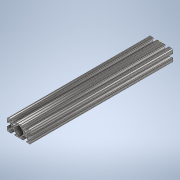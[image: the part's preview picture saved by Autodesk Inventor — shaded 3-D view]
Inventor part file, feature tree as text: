
AUTODESK INVENTOR PART (.ipt)
format: ipt  version: 2020 (Build 240168000, 168)  size: 344,576 bytes
history: native  units: in
note: dims shown in document units (in); Inventor stores cm internally (conversion verified against a paired STEP export)
features: sketch x2, extrude x1
ambient origin geometry x8: Origin, YZ Plane, XZ Plane, XY Plane, X Axis, Y Axis, Z Axis, Center Point
bodies: Solid1 (feature_tree)
feature tree (3):
  extrude  "Extrusion1"  [1 undecoded]
  sketch  "Sketch2"
  sketch  "Sketch1"  dims[d0=12.0in d1=0.0in]
note: 1 required parameter value undecoded (feature->parameter linkage not recoverable at this tier; creation-order binding heuristic only, values carry confidence <= 0.55)
